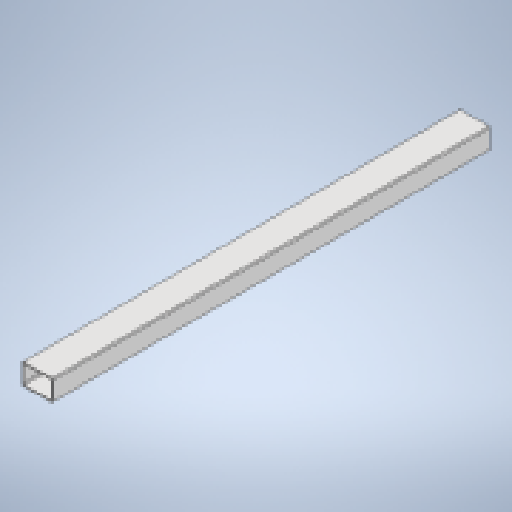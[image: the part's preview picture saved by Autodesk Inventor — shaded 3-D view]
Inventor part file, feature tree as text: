
AUTODESK INVENTOR PART (.ipt)
format: ipt  version: 2023 (Build 270158000, 158)  size: 151,552 bytes
history: native  units: in
note: dims shown in document units (in); Inventor stores cm internally (conversion verified against a paired STEP export)
features: extrude x1, shell x1, fillet x1, sketch x1
ambient origin geometry x8: Origin, YZ Plane, XZ Plane, XY Plane, X Axis, Y Axis, Z Axis, Center Point
bodies: Solid1 (feature_tree)
feature tree (4):
  extrude  "Extrusion1"  Depth=2.0in
  shell  "Shell1"  Thickness=42.0in
  fillet  "Fillet1"  Radius=0.125in
  sketch  "Sketch1"  dims[d0=3.0in d1=2.0in d2=42.0in d3=0.0in d4=0.125in d5=0.125in]
